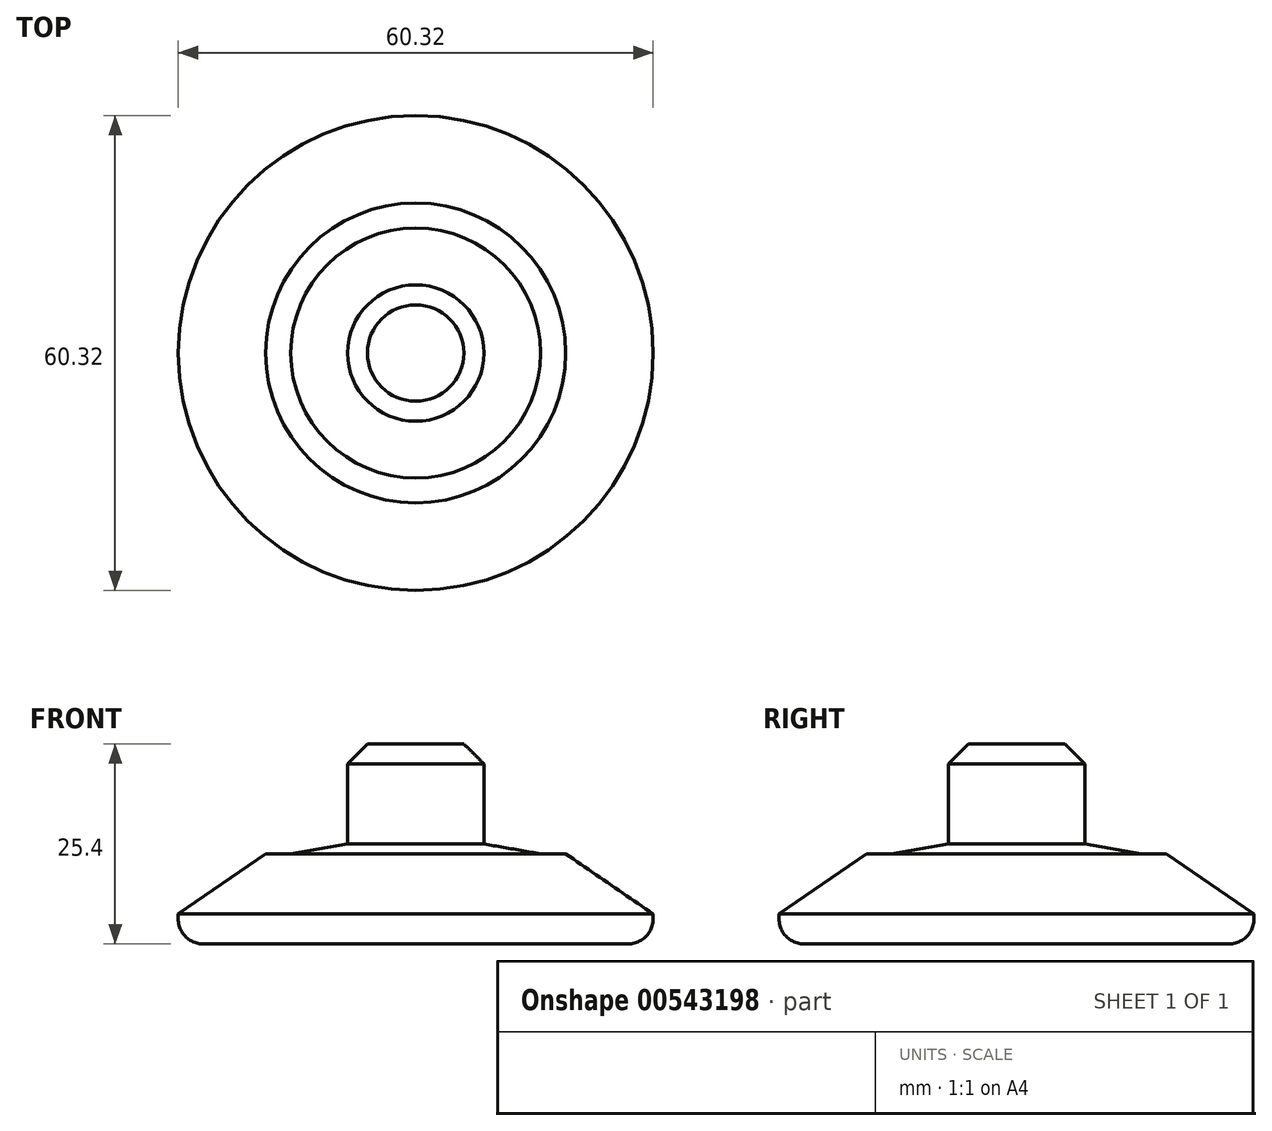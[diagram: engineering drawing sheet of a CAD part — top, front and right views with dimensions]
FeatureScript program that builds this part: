
annotation { "Feature Type Name" : "Feature", "Feature Type Description" : "" }
export const myFeature = defineFeature(function(context is Context, id is Id, definition is map)
    precondition{}
    {
        {
            var Q0;
            Q0=qCreatedBy(makeId("Front.planeOp"),FACE);
            var sketch = newSketch(context, id + "F0", { "sketchPlane" : qUnion([Q0])});
            skLineSegment(sketch, "E0", {"start": v(0, 13) * mm, "end": v(8.66, 13) * mm});
            skLineSegment(sketch, "E1", {"start": v(8.66, 13) * mm, "end": v(8.66, 0.3) * mm});
            skLineSegment(sketch, "E2", {"start": v(8.66, 0.3) * mm, "end": v(15.88, -0.97) * mm});
            skLineSegment(sketch, "E3", {"start": v(15.88, -0.97) * mm, "end": v(19.05, -0.97) * mm});
            skLineSegment(sketch, "E4", {"start": v(30.16, -8.59) * mm, "end": v(30.16, -12.4) * mm});
            skLineSegment(sketch, "E5", {"start": v(30.16, -12.4) * mm, "end": v(0, -12.4) * mm});
            skLineSegment(sketch, "E6", {"start": v(0, -12.4) * mm, "end": v(0, 13) * mm});
            skLineSegment(sketch, "E7", {"start": v(0, 26.06) * mm, "end": v(0, -22.4) * mm, "construction": true});
            skPoint(sketch, "E8", {"position": v(30.16, -8.59) * mm});
            skPoint(sketch, "E9", {"position": v(19.05, -0.97) * mm});
            skLineSegment(sketch, "E10", {"start": v(19.05, -0.97) * mm, "end": v(30.16, -8.59) * mm});
            skSolve(sketch);
        }
        {
            var Q0;
            Q0=makeQuery(id+"F0.imprint","IMPRINT",FACE,{"disambiguationData":[TD([[makeQuery(id+"F0.imprint","IMPRINT",EDGE,{"derivedFrom":sQuery(id+"F0.wireOp",EDGE,"E0")}),-1.0]])]});
            var Q1;
            Q1=sQuery(id+"F0.wireOp",EDGE,"E7");
            revolve(context, id + "F1", {"entities" : qUnion([Q0]), "axis" : qUnion([Q1]), "revolveType" : RevolveType.FULL});
        }
        {
            var Q0;
            Q0=makeQuery(id+"F1.opRevolve","SWEPT_EDGE",EDGE,{"disambiguationData":[OSD([sQuery(id+"F0.wireOp",EDGE,"E0"),sQuery(id+"F0.wireOp",EDGE,"E1")])]});
            chamfer(context, id + "F2", {"entities" : qUnion([Q0]), "width" : 2.54 * mm, "tangentPropagation" : true});
        }
        {
            var Q0;
            Q0=makeQuery(id+"F1.opRevolve","SWEPT_EDGE",EDGE,{"disambiguationData":[OSD([sQuery(id+"F0.wireOp",EDGE,"E4"),sQuery(id+"F0.wireOp",EDGE,"E5")])]});
            fillet(context, id + "F3", {"entities" : qUnion([Q0]), "radius" : 3.17 * mm, "tangentPropagation" : true, "allowEdgeOverflow" : false});
        }
    });
